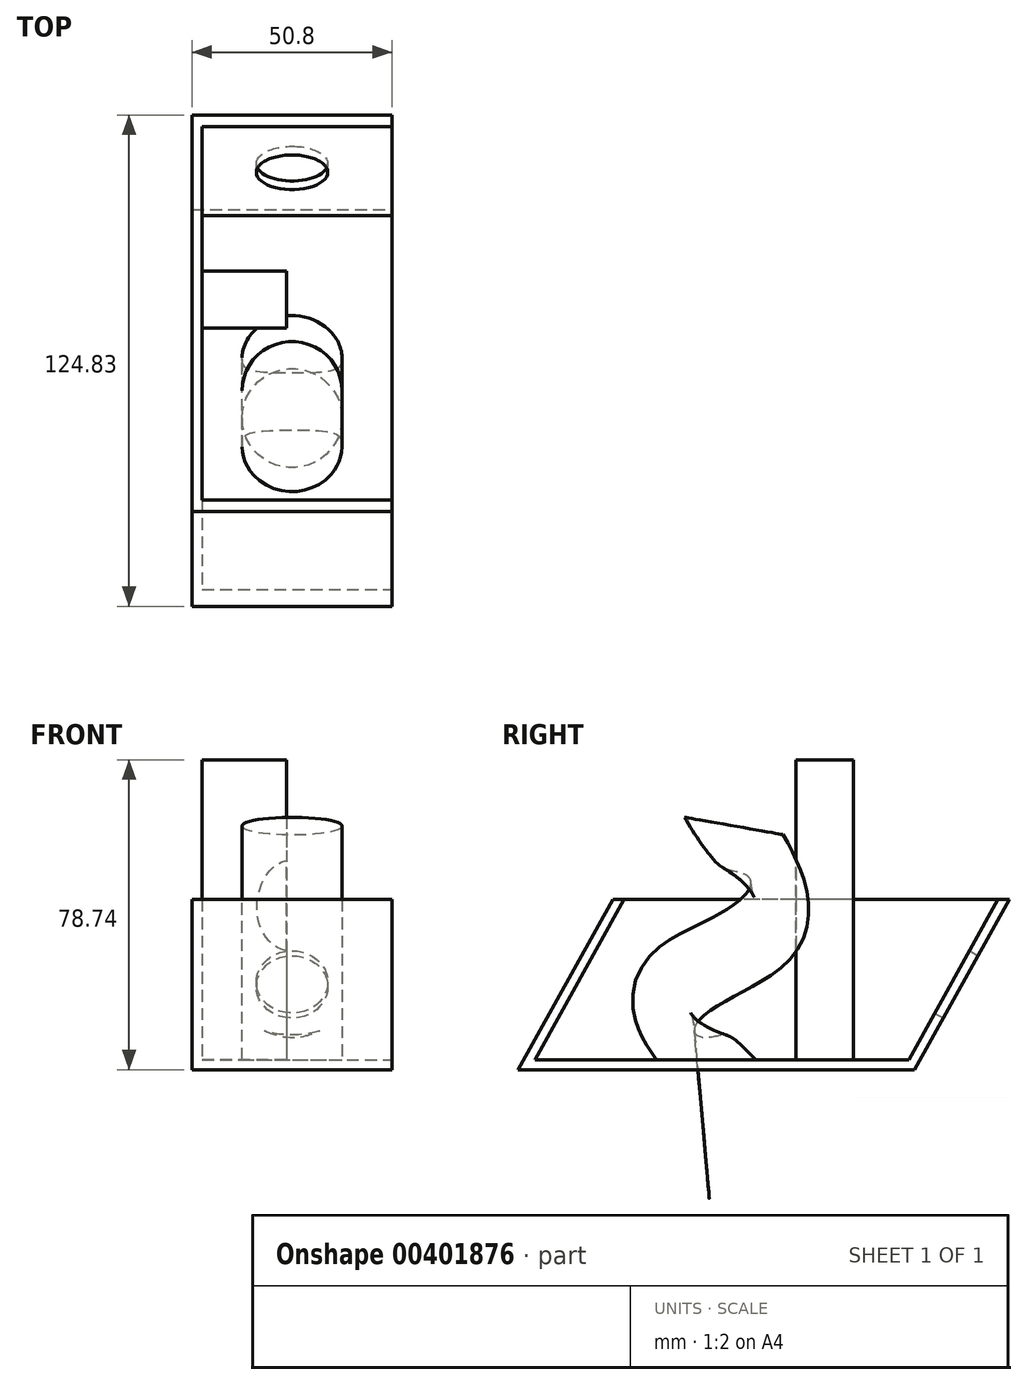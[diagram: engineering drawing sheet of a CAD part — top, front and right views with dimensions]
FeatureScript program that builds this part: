
annotation { "Feature Type Name" : "Feature", "Feature Type Description" : "" }
export const myFeature = defineFeature(function(context is Context, id is Id, definition is map)
    precondition{}
    {
        {
            var Q0;
            Q0=qCreatedBy(makeId("Right.planeOp"),FACE);
            var sketch = newSketch(context, id + "F0", { "sketchPlane" : qUnion([Q0])});
            skLineSegment(sketch, "E0", {"start": v(-26.75, 43.23) * mm, "end": v(-50.82, 0) * mm});
            skLineSegment(sketch, "E1", {"start": v(-50.82, 0) * mm, "end": v(49.93, 0) * mm});
            skLineSegment(sketch, "E2", {"start": v(49.93, 0) * mm, "end": v(74, 43.23) * mm});
            skLineSegment(sketch, "E3", {"start": v(74, 43.23) * mm, "end": v(-26.75, 43.23) * mm});
            skSolve(sketch);
        }
        {
            var Q0;
            Q0=makeQuery(id+"F0.imprint","IMPRINT",FACE,{"disambiguationData":[TD([[makeQuery(id+"F0.imprint","IMPRINT",EDGE,{"derivedFrom":sQuery(id+"F0.wireOp",EDGE,"E0")}),1.0]])]});
            extrude(context, id + "F1", {"entities" : qUnion([Q0]), "oppositeDirection" : true, "depth" : 50.8 * mm});
        }
        {
            var Q0;
            Q0=makeQuery(id+"F1.opExtrude","SWEPT_FACE",FACE,{"disambiguationData":[OSD([sQuery(id+"F0.wireOp",EDGE,"E3")])]});
            var Q1;
            Q1=makeQuery(id+"F1.opExtrude","CAP_FACE",FACE,{"disambiguationData":[OSD([sQuery(id+"F0.wireOp",EDGE,"E0"),sQuery(id+"F0.wireOp",EDGE,"E1"),sQuery(id+"F0.wireOp",EDGE,"E2"),sQuery(id+"F0.wireOp",EDGE,"E3")])],"isStart":true});
            shell(context, id + "F2", {"entities" : qUnion([Q0, Q1]), "thickness" : 2.54 * mm});
        }
        {
            var Q0;
            Q0=makeQuery(id+"F1.opExtrude","SWEPT_FACE",FACE,{"disambiguationData":[OSD([sQuery(id+"F0.wireOp",EDGE,"E2")])]});
            var sketch = newSketch(context, id + "F3", { "sketchPlane" : qUnion([Q0])});
            skCircle(sketch, "E4", {"center": v(25.4, 48.38) * mm, "radius": 9.07 * mm});
            skPoint(sketch, "E4.centerSnap0", {"position": v(0, 49.03) * mm});
            skSolve(sketch);
        }
        {
            var Q0;
            Q0 = qSketchRegion(id + "F3", true);
            extrude(context, id + "F4", {"entities" : qUnion([Q0]), "operationType" : NewBodyOperationType.REMOVE, "oppositeDirection" : true, "depth" : 25.4 * mm});
        }
        {
            var Q0;
            Q0=makeQuery(id+"F1.opExtrude","SWEPT_FACE",FACE,{"disambiguationData":[OSD([sQuery(id+"F0.wireOp",EDGE,"E1")])]});
            var sketch = newSketch(context, id + "F5", { "sketchPlane" : qUnion([Q0])});
            skCircle(sketch, "E5", {"center": v(-25.4, 0.87) * mm, "radius": 12.7 * mm});
            skPoint(sketch, "E5.centerSnap0", {"position": v(-25.4, 50.82) * mm});
            skSolve(sketch);
        }
        {
            var Q0;
            Q0=qCreatedBy(makeId("Right.planeOp"),FACE);
            var sketch = newSketch(context, id + "F6", { "sketchPlane" : qUnion([Q0])});
            skFitSpline(sketch, "E6", {"points": [v(0, 0) * mm, v(-9.03, 19.08) * mm, v(11.64, 36.7) * mm, v(4.8, 61.78) * mm], "startDerivative": vector(-56.5, 66.26) * mm, "endDerivative": vector(-47.21, 80.22) * mm});
            skSolve(sketch);
        }
        {
            var Q0;
            Q0=makeQuery(id+"F5.imprint","IMPRINT",FACE,{"disambiguationData":[TD([[makeQuery(id+"F5.imprint","IMPRINT",EDGE,{"derivedFrom":sQuery(id+"F5.wireOp",EDGE,"E5")}),1.0]])]});
            var Q1;
            Q1=sQuery(id+"F6.wireOp",EDGE,"E6");
            sweep(context, id + "F7", {"operationType" : NewBodyOperationType.ADD, "profiles" : qUnion([Q0]), "path" : qUnion([Q1])});
        }
        {
            var Q0;
            Q0=makeQuery(id+"F2.opShell","OFFSET_FACE",FACE,{"disambiguationData":[OSD([sQuery(id+"F0.wireOp",EDGE,"E1")])]});
            var sketch = newSketch(context, id + "F8", { "sketchPlane" : qUnion([Q0])});
            skLineSegment(sketch, "E7", {"start": v(-26.83, 19.84) * mm, "end": v(-26.83, 34.36) * mm});
            skLineSegment(sketch, "E8", {"start": v(-26.83, 34.36) * mm, "end": v(-48.26, 34.36) * mm});
            skLineSegment(sketch, "E9", {"start": v(-26.83, 19.84) * mm, "end": v(-48.26, 19.84) * mm});
            skLineSegment(sketch, "E10", {"start": v(-48.26, 19.84) * mm, "end": v(-48.26, 34.36) * mm});
            skSolve(sketch);
        }
        {
            var Q0;
            Q0=makeQuery(id+"F8.imprint","IMPRINT",FACE,{"disambiguationData":[TD([[makeQuery(id+"F8.imprint","IMPRINT",EDGE,{"derivedFrom":sQuery(id+"F8.wireOp",EDGE,"E7")}),1.0]])]});
            extrude(context, id + "F9", {"entities" : qUnion([Q0]), "operationType" : NewBodyOperationType.ADD, "depth" : 76.2 * mm});
        }
    });
